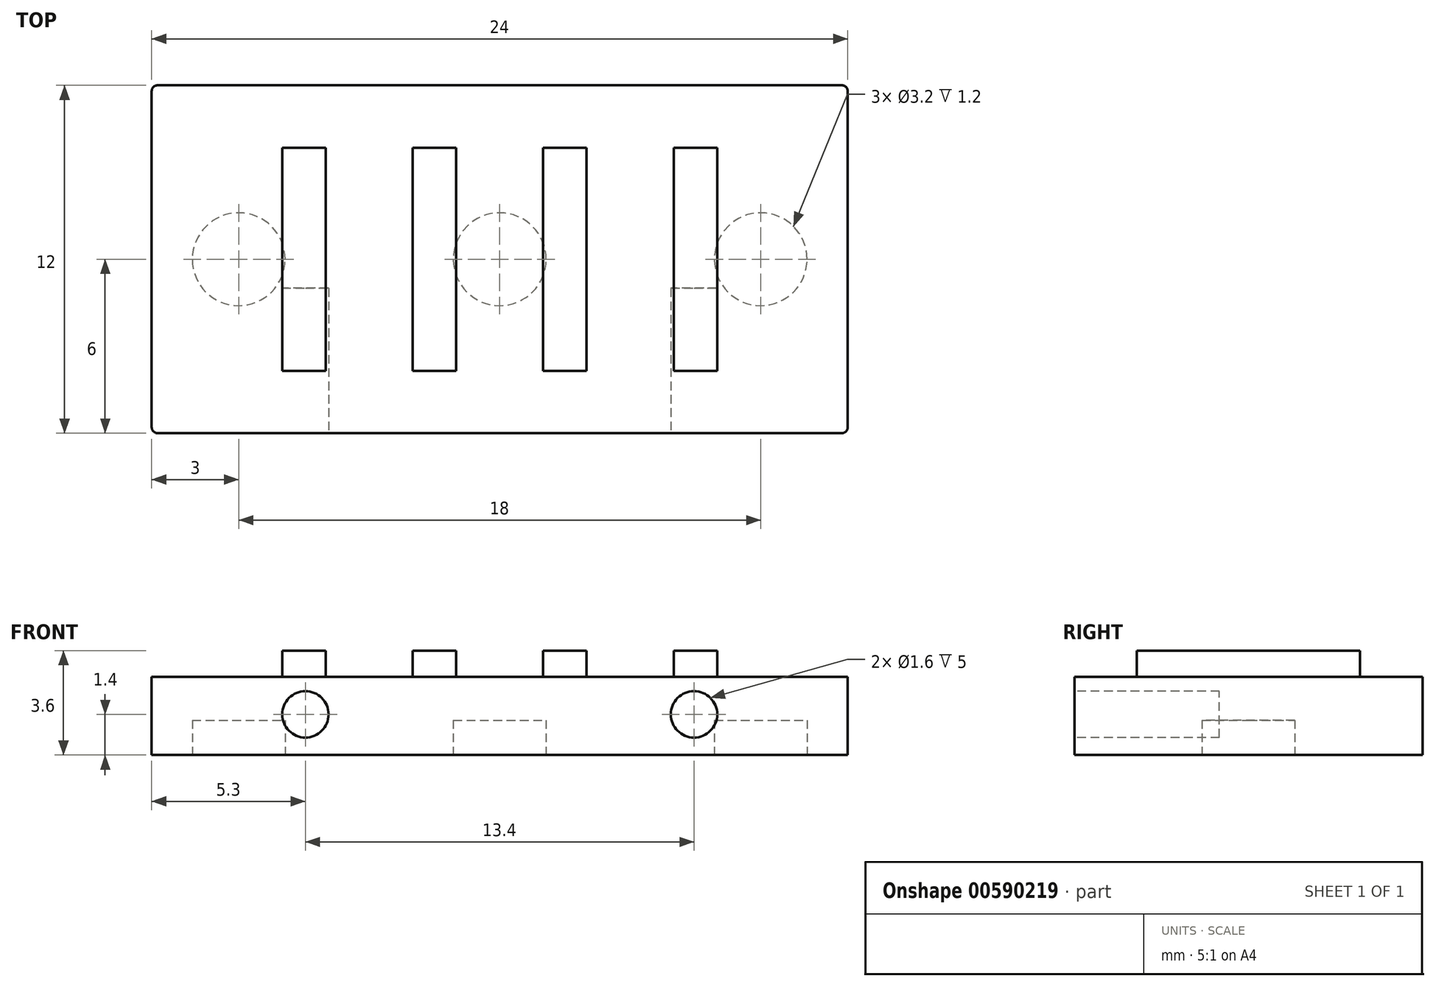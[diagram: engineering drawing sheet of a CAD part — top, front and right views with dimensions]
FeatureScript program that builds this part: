
annotation { "Feature Type Name" : "Feature", "Feature Type Description" : "" }
export const myFeature = defineFeature(function(context is Context, id is Id, definition is map)
    precondition{}
    {
        {
            var Q0;
            Q0=qCreatedBy(makeId("Top.planeOp"),FACE);
            var sketch = newSketch(context, id + "F0", { "sketchPlane" : qUnion([Q0])});
            skLineSegment(sketch, "E0.bottom", {"start": v(-10.5, 3.85) * mm, "end": v(10.5, 3.85) * mm});
            skLineSegment(sketch, "E0.top", {"start": v(-10.5, -3.85) * mm, "end": v(10.5, -3.85) * mm});
            skLineSegment(sketch, "E0.left", {"start": v(-10.5, 3.85) * mm, "end": v(-10.5, -3.85) * mm});
            skLineSegment(sketch, "E0.right", {"start": v(10.5, 3.85) * mm, "end": v(10.5, -3.85) * mm});
            skPoint(sketch, "E0.middle", {"position": v(0, 0) * mm});
            skLineSegment(sketch, "E1", {"start": v(-7.5, 3.85) * mm, "end": v(-7.5, -3.85) * mm});
            skLineSegment(sketch, "E2", {"start": v(-6, 3.85) * mm, "end": v(-6, -3.85) * mm});
            skLineSegment(sketch, "E3", {"start": v(-1.5, 3.85) * mm, "end": v(-1.5, -3.85) * mm});
            skLineSegment(sketch, "E4", {"start": v(1.5, 3.85) * mm, "end": v(1.5, -3.85) * mm});
            skLineSegment(sketch, "E5", {"start": v(3, 3.85) * mm, "end": v(3, -3.85) * mm});
            skLineSegment(sketch, "E6", {"start": v(6, 3.85) * mm, "end": v(6, -3.85) * mm});
            skLineSegment(sketch, "E7", {"start": v(1.5, 3.85) * mm, "end": v(-1.5, -3.85) * mm, "construction": true});
            skLineSegment(sketch, "E8.bottom", {"start": v(-12, 6) * mm, "end": v(12, 6) * mm});
            skLineSegment(sketch, "E8.top", {"start": v(-12, -6) * mm, "end": v(12, -6) * mm});
            skLineSegment(sketch, "E8.left", {"start": v(-12, 6) * mm, "end": v(-12, -6) * mm});
            skLineSegment(sketch, "E8.right", {"start": v(12, 6) * mm, "end": v(12, -6) * mm});
            skLineSegment(sketch, "E9", {"start": v(-3, 3.85) * mm, "end": v(-3, -3.85) * mm});
            skLineSegment(sketch, "E10", {"start": v(7.5, 3.85) * mm, "end": v(7.5, -3.85) * mm});
            skSolve(sketch);
        }
        {
            var Q0;
            {var subQ0=sQuery(id+"F0.wireOp",EDGE,"E1");Q0=makeQuery(id+"F0.imprint","IMPRINT",FACE,{"disambiguationData":[TD([[makeQuery(id+"F0.imprint","IMPRINT",EDGE,{"derivedFrom":subQ0}),1.0]])]});}
            var Q1;
            {var subQ0=sQuery(id+"F0.wireOp",EDGE,"E3");Q1=makeQuery(id+"F0.imprint","IMPRINT",FACE,{"disambiguationData":[TD([[makeQuery(id+"F0.imprint","IMPRINT",EDGE,{"derivedFrom":subQ0}),-1.0]])]});}
            var Q2;
            {var subQ0=sQuery(id+"F0.wireOp",EDGE,"E4");Q2=makeQuery(id+"F0.imprint","IMPRINT",FACE,{"disambiguationData":[TD([[makeQuery(id+"F0.imprint","IMPRINT",EDGE,{"derivedFrom":subQ0}),1.0]])]});}
            var Q3;
            {var subQ0=sQuery(id+"F0.wireOp",EDGE,"E6");Q3=makeQuery(id+"F0.imprint","IMPRINT",FACE,{"disambiguationData":[TD([[makeQuery(id+"F0.imprint","IMPRINT",EDGE,{"derivedFrom":subQ0}),1.0]])]});}
            var Q4;
            {var subQ1=sQuery(id+"F0.wireOp",EDGE,"E0.left");Q4=makeQuery(id+"F0.imprint","IMPRINT",FACE,{"disambiguationData":[TD([[makeQuery(id+"F0.imprint","IMPRINT",EDGE,{"derivedFrom":subQ1}),-1.0]])]});}
            extrude(context, id + "F1", {"entities" : qUnion([Q0, Q1, Q2, Q3, Q4]), "depth" : .9 * mm, "offsetDistance" : 25 * mm});
        }
        {
            var Q0;
            Q0=makeQuery(id+"F1.opExtrude","CAP_FACE",FACE,{"disambiguationData":[OSD([sQuery(id+"F0.wireOp",EDGE,"E0.bottom"),sQuery(id+"F0.wireOp",EDGE,"E0.top"),sQuery(id+"F0.wireOp",EDGE,"E0.left"),sQuery(id+"F0.wireOp",EDGE,"E0.right"),sQuery(id+"F0.wireOp",EDGE,"E1"),sQuery(id+"F0.wireOp",EDGE,"E2"),sQuery(id+"F0.wireOp",EDGE,"E3"),sQuery(id+"F0.wireOp",EDGE,"E4"),sQuery(id+"F0.wireOp",EDGE,"E5"),sQuery(id+"F0.wireOp",EDGE,"E6"),sQuery(id+"F0.wireOp",EDGE,"E8.bottom"),sQuery(id+"F0.wireOp",EDGE,"E8.top"),sQuery(id+"F0.wireOp",EDGE,"E8.left"),sQuery(id+"F0.wireOp",EDGE,"E8.right"),sQuery(id+"F0.wireOp",EDGE,"E9"),sQuery(id+"F0.wireOp",EDGE,"E10")])],"isStart":true});
            var sketch = newSketch(context, id + "F2", { "sketchPlane" : qUnion([Q0])});
            skLineSegment(sketch, "E11.bottom", {"start": v(12, 6) * mm, "end": v(-12, 6) * mm});
            skLineSegment(sketch, "E11.top", {"start": v(12, -6) * mm, "end": v(-12, -6) * mm});
            skLineSegment(sketch, "E11.left", {"start": v(12, 6) * mm, "end": v(12, -6) * mm});
            skLineSegment(sketch, "E11.right", {"start": v(-12, 6) * mm, "end": v(-12, -6) * mm});
            skPoint(sketch, "E11.middle", {"position": v(0, 0) * mm});
            skSolve(sketch);
        }
        {
            var Q0;
            Q0 = qSketchRegion(id + "F2", true);
            extrude(context, id + "F3", {"entities" : qUnion([Q0]), "operationType" : NewBodyOperationType.ADD, "depth" : 2.7 * mm, "offsetDistance" : 25 * mm});
        }
        {
            var Q0;
            Q0=makeQuery(id+"F3.opExtrude","CAP_FACE",FACE,{"disambiguationData":[OSD([sQuery(id+"F2.wireOp",EDGE,"E11.bottom"),sQuery(id+"F2.wireOp",EDGE,"E11.top"),sQuery(id+"F2.wireOp",EDGE,"E11.left"),sQuery(id+"F2.wireOp",EDGE,"E11.right")])],"isStart":false});
            var sketch = newSketch(context, id + "F4", { "sketchPlane" : qUnion([Q0])});
            skCircle(sketch, "E12", {"center": v(0, 0) * mm, "radius": 1.6 * mm});
            skCircle(sketch, "E13", {"center": v(9, 0) * mm, "radius": 1.6 * mm});
            skCircle(sketch, "E14", {"center": v(-9, 0) * mm, "radius": 1.6 * mm});
            skSolve(sketch);
        }
        {
            var Q0;
            Q0 = qSketchRegion(id + "F4", true);
            extrude(context, id + "F5", {"entities" : qUnion([Q0]), "operationType" : NewBodyOperationType.REMOVE, "oppositeDirection" : true, "depth" : 1.2 * mm, "offsetDistance" : 25 * mm});
        }
        {
            var Q0;
            Q0=makeQuery(id+"F3.boolean.opBoolean","MERGE",EDGE,{"derivedFrom":[makeQuery(id+"F1.opExtrude","SWEPT_EDGE",EDGE,{"disambiguationData":[OSD([sQuery(id+"F0.wireOp",EDGE,"E8.top"),sQuery(id+"F0.wireOp",EDGE,"E8.left")])]}),makeQuery(id+"F3.opExtrude","SWEPT_EDGE",EDGE,{"disambiguationData":[OSD([sQuery(id+"F2.wireOp",EDGE,"E11.bottom"),sQuery(id+"F2.wireOp",EDGE,"E11.right")])]})]});
            var Q1;
            Q1=makeQuery(id+"F3.boolean.opBoolean","MERGE",EDGE,{"derivedFrom":[makeQuery(id+"F1.opExtrude","SWEPT_EDGE",EDGE,{"disambiguationData":[OSD([sQuery(id+"F0.wireOp",EDGE,"E8.top"),sQuery(id+"F0.wireOp",EDGE,"E8.right")])]}),makeQuery(id+"F3.opExtrude","SWEPT_EDGE",EDGE,{"disambiguationData":[OSD([sQuery(id+"F2.wireOp",EDGE,"E11.bottom"),sQuery(id+"F2.wireOp",EDGE,"E11.left")])]})]});
            var Q2;
            Q2=makeQuery(id+"F3.boolean.opBoolean","MERGE",EDGE,{"derivedFrom":[makeQuery(id+"F1.opExtrude","SWEPT_EDGE",EDGE,{"disambiguationData":[OSD([sQuery(id+"F0.wireOp",EDGE,"E8.bottom"),sQuery(id+"F0.wireOp",EDGE,"E8.right")])]}),makeQuery(id+"F3.opExtrude","SWEPT_EDGE",EDGE,{"disambiguationData":[OSD([sQuery(id+"F2.wireOp",EDGE,"E11.top"),sQuery(id+"F2.wireOp",EDGE,"E11.left")])]})]});
            var Q3;
            Q3=makeQuery(id+"F3.boolean.opBoolean","MERGE",EDGE,{"derivedFrom":[makeQuery(id+"F1.opExtrude","SWEPT_EDGE",EDGE,{"disambiguationData":[OSD([sQuery(id+"F0.wireOp",EDGE,"E8.bottom"),sQuery(id+"F0.wireOp",EDGE,"E8.left")])]}),makeQuery(id+"F3.opExtrude","SWEPT_EDGE",EDGE,{"disambiguationData":[OSD([sQuery(id+"F2.wireOp",EDGE,"E11.top"),sQuery(id+"F2.wireOp",EDGE,"E11.right")])]})]});
            fillet(context, id + "F6", {"entities" : qUnion([Q0, Q1, Q2, Q3]), "radius" : .2 * mm, "tangentPropagation" : true, "allowEdgeOverflow" : false});
        }
        {
            var Q0;
            Q0=makeQuery(id+"F3.boolean.opBoolean","MERGE",FACE,{"derivedFrom":[makeQuery(id+"F1.opExtrude","SWEPT_FACE",FACE,{"disambiguationData":[OSD([sQuery(id+"F0.wireOp",EDGE,"E8.top")])]}),makeQuery(id+"F3.opExtrude","SWEPT_FACE",FACE,{"disambiguationData":[OSD([sQuery(id+"F2.wireOp",EDGE,"E11.bottom")])]})]});
            var sketch = newSketch(context, id + "F7", { "sketchPlane" : qUnion([Q0])});
            skCircle(sketch, "E15", {"center": v(-6.7, -1.3) * mm, "radius": 0.8 * mm});
            skCircle(sketch, "E16", {"center": v(6.7, -1.3) * mm, "radius": 0.8 * mm});
            skSolve(sketch);
        }
        {
            var Q0;
            Q0 = qSketchRegion(id + "F7", true);
            extrude(context, id + "F8", {"entities" : qUnion([Q0]), "operationType" : NewBodyOperationType.REMOVE, "oppositeDirection" : true, "depth" : 5 * mm, "offsetDistance" : 25 * mm});
        }
    });
